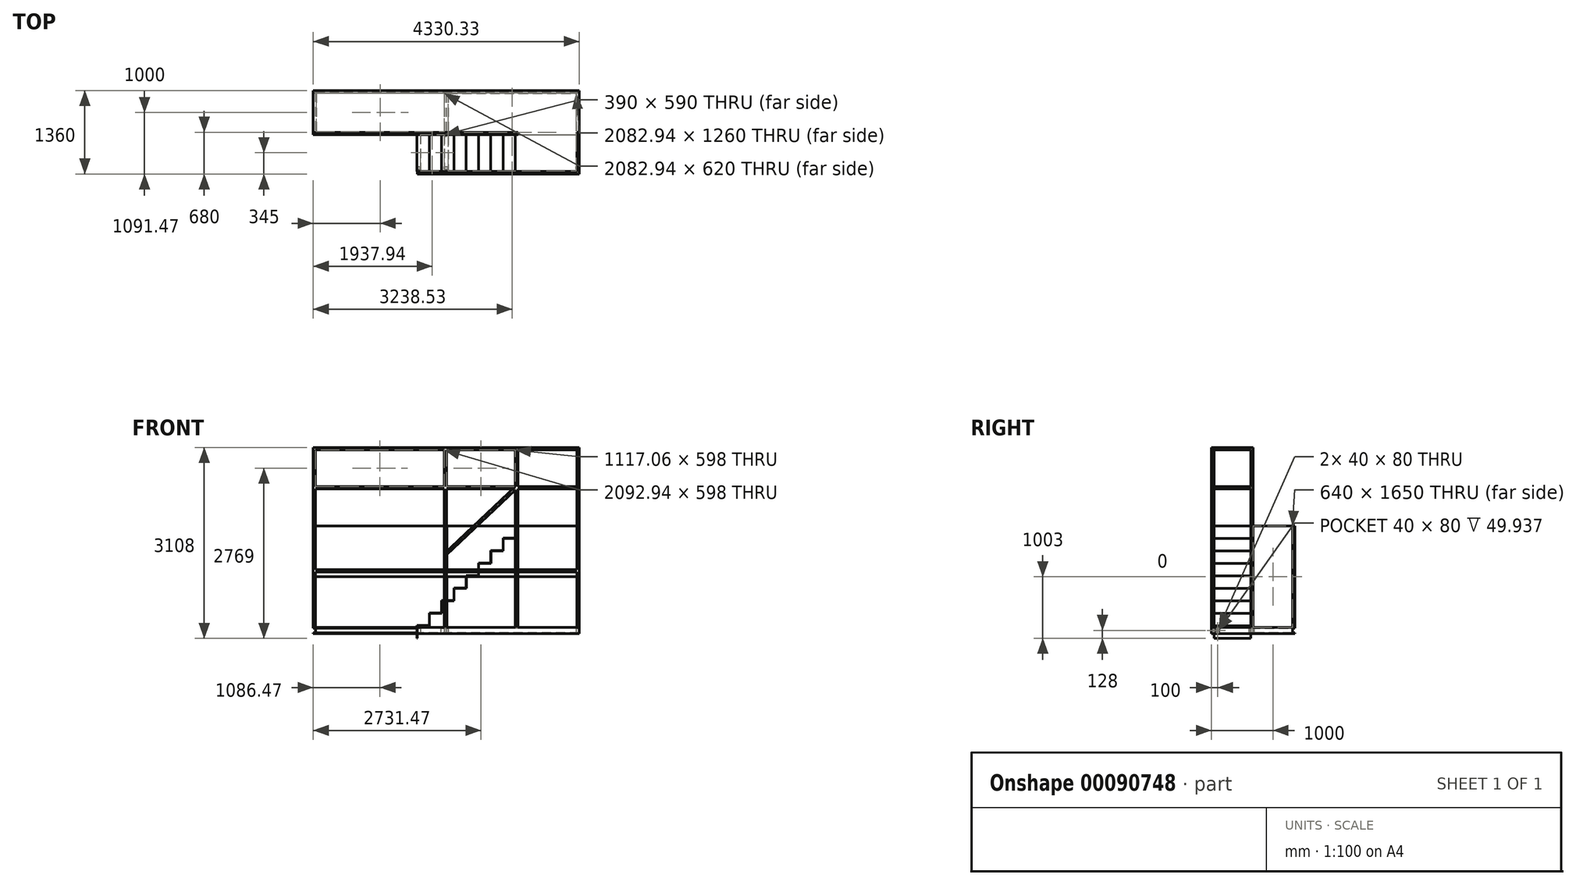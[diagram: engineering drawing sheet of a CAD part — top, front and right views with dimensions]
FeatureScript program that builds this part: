
annotation { "Feature Type Name" : "Feature", "Feature Type Description" : "" }
export const myFeature = defineFeature(function(context is Context, id is Id, definition is map)
    precondition{}
    {
        {
            var Q0;
            Q0=qCreatedBy(makeId("Top.planeOp"),FACE);
            var sketch = newSketch(context, id + "F0", { "sketchPlane" : qUnion([Q0])});
            skLineSegment(sketch, "E0.rect.bottom", {"start": v(2165, 680) * mm, "end": v(-2165, 680) * mm});
            skLineSegment(sketch, "E0.rect.top", {"start": v(2165, -680) * mm, "end": v(-32.06, -680) * mm});
            skLineSegment(sketch, "E0.rect.left", {"start": v(2165, 680) * mm, "end": v(2165, -680) * mm});
            skLineSegment(sketch, "E0.rect.right", {"start": v(-2165, 680) * mm, "end": v(-2165, -40) * mm});
            skPoint(sketch, "E0.rect.middle", {"position": v(0, 0) * mm});
            skLineSegment(sketch, "E1.rect.top", {"start": v(2115, -630) * mm, "end": v(32.06, -630) * mm});
            skLineSegment(sketch, "E1.rect.right", {"start": v(-2115, 630) * mm, "end": v(-2115, 10) * mm});
            skLineSegment(sketch, "E2.rect.left", {"start": v(32.06, -10) * mm, "end": v(32.06, -630) * mm});
            skLineSegment(sketch, "E2.rect.right", {"start": v(-32.06, 630) * mm, "end": v(-32.06, -680) * mm});
            skLineSegment(sketch, "E3.trimOffspring", {"start": v(-32.06, 630) * mm, "end": v(-2115, 630) * mm});
            skLineSegment(sketch, "E4", {"start": v(-2115, 10) * mm, "end": v(-32.06, 10) * mm});
            skLineSegment(sketch, "E5", {"start": v(-2165, -40) * mm, "end": v(-32.06, -40) * mm});
            skLineSegment(sketch, "E6", {"start": v(32.06, 630) * mm, "end": v(2115, 630) * mm});
            skLineSegment(sketch, "E7", {"start": v(2115, 630) * mm, "end": v(2115, -630) * mm});
            skLineSegment(sketch, "E8", {"start": v(32.06, 630) * mm, "end": v(32.06, -10) * mm});
            skLineSegment(sketch, "E9", {"start": v(-32.06, -680) * mm, "end": v(-472.06, -680) * mm});
            skLineSegment(sketch, "E10", {"start": v(-472.06, -680) * mm, "end": v(-472.06, -630) * mm});
            skLineSegment(sketch, "E11", {"start": v(-472.06, -630) * mm, "end": v(-32.06, -630) * mm});
            skLineSegment(sketch, "E12", {"start": v(-472.06, -630) * mm, "end": v(-472.06, -40) * mm});
            skLineSegment(sketch, "E13", {"start": v(-472.06, -40) * mm, "end": v(-422.06, -40) * mm});
            skLineSegment(sketch, "E14", {"start": v(-422.06, -40) * mm, "end": v(-422.06, -630) * mm});
            skSolve(sketch);
        }
        {
            var Q0;
            Q0=makeQuery(id+"F0.imprint","IMPRINT",FACE,{"disambiguationData":[TD([[makeQuery(id+"F0.imprint","IMPRINT",EDGE,{"derivedFrom":sQuery(id+"F0.wireOp",EDGE,"E0.rect.bottom")}),1.0]])]});
            var Q1;
            {var subQ0=sQuery(id+"F0.wireOp",EDGE,"E4");Q1=makeQuery(id+"F0.imprint","IMPRINT",FACE,{"disambiguationData":[TD([[makeQuery(id+"F0.imprint","IMPRINT",EDGE,{"derivedFrom":subQ0}),-1.0]])]});}
            var Q2;
            {var subQ0=sQuery(id+"F0.wireOp",EDGE,"E12");Q2=makeQuery(id+"F0.imprint","IMPRINT",FACE,{"disambiguationData":[TD([[makeQuery(id+"F0.imprint","IMPRINT",EDGE,{"derivedFrom":subQ0}),-1.0]])]});}
            var Q3;
            {var subQ3=sQuery(id+"F0.wireOp",EDGE,"E9");Q3=makeQuery(id+"F0.imprint","IMPRINT",FACE,{"disambiguationData":[TD([[makeQuery(id+"F0.imprint","IMPRINT",EDGE,{"derivedFrom":subQ3}),-1.0]])]});}
            extrude(context, id + "F1", {"entities" : qUnion([Q0, Q1, Q2, Q3]), "depth" : 100 * mm});
        }
        {
            var Q0;
            Q0=makeQuery(id+"F1.opExtrude","SWEPT_FACE",FACE,{"disambiguationData":[OSD([sQuery(id+"F0.wireOp",EDGE,"E0.rect.right")])]});
            var sketch = newSketch(context, id + "F2", { "sketchPlane" : qUnion([Q0])});
            skLineSegment(sketch, "E15.bottom", {"start": v(-680, 90) * mm, "end": v(-640, 90) * mm});
            skLineSegment(sketch, "E15.top", {"start": v(-680, 10) * mm, "end": v(-640, 10) * mm});
            skLineSegment(sketch, "E15.left", {"start": v(-680, 90) * mm, "end": v(-680, 10) * mm});
            skLineSegment(sketch, "E15.right", {"start": v(-640, 90) * mm, "end": v(-640, 10) * mm});
            skLineSegment(sketch, "E16.bottom", {"start": v(40, 90) * mm, "end": v(0, 90) * mm});
            skLineSegment(sketch, "E16.top", {"start": v(40, 10) * mm, "end": v(0, 10) * mm});
            skLineSegment(sketch, "E16.left", {"start": v(40, 90) * mm, "end": v(40, 10) * mm});
            skLineSegment(sketch, "E16.right", {"start": v(0, 90) * mm, "end": v(0, 10) * mm});
            skSolve(sketch);
        }
        {
            var Q0;
            Q0=makeQuery(id+"F2.imprint","IMPRINT",FACE,{"disambiguationData":[TD([[makeQuery(id+"F2.imprint","IMPRINT",EDGE,{"derivedFrom":sQuery(id+"F2.wireOp",EDGE,"E16.bottom")}),1.0]])]});
            var Q1;
            Q1=makeQuery(id+"F1.opExtrude","SWEPT_FACE",FACE,{"disambiguationData":[OSD([sQuery(id+"F0.wireOp",EDGE,"E10"),sQuery(id+"F0.wireOp",EDGE,"E12")])]});
            extrude(context, id + "F3", {"entities" : qUnion([Q0]), "operationType" : NewBodyOperationType.REMOVE, "endBound" : BoundingType.UP_TO_SURFACE, "oppositeDirection" : true, "endBoundEntityFace" : qUnion([Q1]), "depth" : 25 * mm});
        }
        {
            var Q0;
            Q0=makeQuery(id+"F2.imprint","IMPRINT",FACE,{"disambiguationData":[TD([[makeQuery(id+"F2.imprint","IMPRINT",EDGE,{"derivedFrom":sQuery(id+"F2.wireOp",EDGE,"E15.bottom")}),-1.0]])]});
            var Q1;
            {var subQ0=sQuery(id+"F0.wireOp",EDGE,"E2.rect.right");Q1=makeQuery(id+"F1.opExtrude","SWEPT_FACE",FACE,{"disambiguationData":[OSD([subQ0]),TDD([makeQuery(id+"F0.imprint","IMPRINT",EDGE,{"disambiguationData":[TD([[makeQuery(id+"F0.imprint","INTERSECT",VERTEX,{"derivedFrom":[sQuery(id+"F0.wireOp",EDGE,"E0.rect.top"),subQ0]}),1.0]])],"derivedFrom":subQ0})])]});}
            extrude(context, id + "F4", {"entities" : qUnion([Q0]), "operationType" : NewBodyOperationType.REMOVE, "endBound" : BoundingType.THROUGH_ALL, "oppositeDirection" : true, "endBoundEntityFace" : qUnion([Q1]), "depth" : 25 * mm});
        }
        {
            var Q0;
            Q0=makeQuery(id+"F3.boolean.opBoolean","COPY",FACE,{"derivedFrom":makeQuery(id+"F3.opExtrude","SWEPT_FACE",FACE,{"disambiguationData":[OSD([sQuery(id+"F2.wireOp",EDGE,"E16.right")])]})});
            var sketch = newSketch(context, id + "F5", { "sketchPlane" : qUnion([Q0])});
            skLineSegment(sketch, "E17.bottom", {"start": v(-2165, 90) * mm, "end": v(-2125, 90) * mm});
            skLineSegment(sketch, "E17.top", {"start": v(-2165, 10) * mm, "end": v(-2125, 10) * mm});
            skLineSegment(sketch, "E17.left", {"start": v(-2165, 90) * mm, "end": v(-2165, 10) * mm});
            skLineSegment(sketch, "E17.right", {"start": v(-2125, 90) * mm, "end": v(-2125, 10) * mm});
            skSolve(sketch);
        }
        {
            var Q0;
            Q0=makeQuery(id+"F5.imprint","IMPRINT",FACE,{"disambiguationData":[TD([[makeQuery(id+"F5.imprint","IMPRINT",EDGE,{"derivedFrom":sQuery(id+"F5.wireOp",EDGE,"4b8e484b-d1e7-4c6f-93f2-1164223cb3a1.bottom")}),1.0]])]});
            var Q1;
            Q1=makeQuery(id+"F5.imprint","IMPRINT",FACE,{"disambiguationData":[TD([[makeQuery(id+"F5.imprint","IMPRINT",EDGE,{"derivedFrom":sQuery(id+"F5.wireOp",EDGE,"E17.bottom")}),1.0]])]});
            var Q2;
            Q2=makeQuery(id+"F1.opExtrude","SWEPT_FACE",FACE,{"disambiguationData":[OSD([sQuery(id+"F0.wireOp",EDGE,"E3.trimOffspring")])]});
            extrude(context, id + "F6", {"entities" : qUnion([Q0, Q1]), "operationType" : NewBodyOperationType.REMOVE, "endBound" : BoundingType.THROUGH_ALL, "oppositeDirection" : true, "endBoundEntityFace" : qUnion([Q2]), "depth" : 25 * mm});
        }
        {
            var Q0;
            Q0=qCreatedBy(makeId("Top.planeOp"),FACE);
            cPlane(context, id + "F7", {"entities" : qUnion([Q0]), "cplaneType" : CPlaneType.OFFSET, "offset" : 1750 * mm, "width" : 150 * mm, "height" : 150 * mm});
        }
        {
            var Q0;
            Q0=qCreatedBy(makeId("Front.planeOp"),FACE);
            var sketch = newSketch(context, id + "F8", { "sketchPlane" : qUnion([Q0])});
            skLineSegment(sketch, "E18.bottom", {"start": v(0, 10) * mm, "end": v(-90, 10) * mm});
            skLineSegment(sketch, "E18.top", {"start": v(0, 90) * mm, "end": v(-90, 90) * mm});
            skLineSegment(sketch, "E18.left", {"start": v(0, 10) * mm, "end": v(0, 90) * mm});
            skLineSegment(sketch, "E18.right", {"start": v(-90, 10) * mm, "end": v(-90, 90) * mm});
            skSolve(sketch);
        }
        {
            var Q0;
            Q0=qSketchRegion(id+"F8",true);
            var Q1;
            Q1=makeQuery(id+"F1.opExtrude","SWEPT_FACE",FACE,{"disambiguationData":[OSD([sQuery(id+"F0.wireOp",EDGE,"E3.trimOffspring")])]});
            extrude(context, id + "F9", {"entities" : qUnion([Q0]), "operationType" : NewBodyOperationType.REMOVE, "endBound" : BoundingType.UP_TO_SURFACE, "oppositeDirection" : true, "endBoundEntityFace" : qUnion([Q1]), "depth" : 25 * mm, "hasSecondDirection" : true, "secondDirectionOppositeDirection" : false, "secondDirectionDepth" : 70 * mm});
        }
        {
            var Q0;
            Q0=makeQuery(id+"F1.opExtrude","CAP_FACE",FACE,{"disambiguationData":[OSD([sQuery(id+"F0.wireOp",EDGE,"E0.rect.bottom"),sQuery(id+"F0.wireOp",EDGE,"E0.rect.top"),sQuery(id+"F0.wireOp",EDGE,"E0.rect.left"),sQuery(id+"F0.wireOp",EDGE,"E0.rect.right"),sQuery(id+"F0.wireOp",EDGE,"E1.rect.bottom"),sQuery(id+"F0.wireOp",EDGE,"E1.rect.top"),sQuery(id+"F0.wireOp",EDGE,"E1.rect.left"),sQuery(id+"F0.wireOp",EDGE,"E1.rect.right"),sQuery(id+"F0.wireOp",EDGE,"E2.rect.left"),sQuery(id+"F0.wireOp",EDGE,"E2.rect.right"),sQuery(id+"F0.wireOp",EDGE,"E3.trimOffspring"),sQuery(id+"F0.wireOp",EDGE,"1f8814e2-eb1b-4eeb-ad56-086a4f51f8e6.trimOffspring")])],"isStart":false});
            var sketch = newSketch(context, id + "F10", { "sketchPlane" : qUnion([Q0])});
            skLineSegment(sketch, "E19.bottom", {"start": v(-2165, 680) * mm, "end": v(-2125, 680) * mm});
            skLineSegment(sketch, "E19.top", {"start": v(-2165, 640) * mm, "end": v(-2125, 640) * mm});
            skLineSegment(sketch, "E19.left", {"start": v(-2165, 680) * mm, "end": v(-2165, 640) * mm});
            skLineSegment(sketch, "E19.right", {"start": v(-2125, 680) * mm, "end": v(-2125, 640) * mm});
            skLineSegment(sketch, "E20.bottom", {"start": v(2165, 680) * mm, "end": v(2125, 680) * mm});
            skLineSegment(sketch, "E20.top", {"start": v(2165, 640) * mm, "end": v(2125, 640) * mm});
            skLineSegment(sketch, "E20.left", {"start": v(2165, 680) * mm, "end": v(2165, 640) * mm});
            skLineSegment(sketch, "E20.right", {"start": v(2125, 680) * mm, "end": v(2125, 640) * mm});
            skLineSegment(sketch, "E21.bottom", {"start": v(-27.06, 680) * mm, "end": v(12.94, 680) * mm});
            skLineSegment(sketch, "E21.top", {"start": v(-27.06, 640) * mm, "end": v(12.94, 640) * mm});
            skLineSegment(sketch, "E21.left", {"start": v(-27.06, 680) * mm, "end": v(-27.06, 640) * mm});
            skLineSegment(sketch, "E21.right", {"start": v(12.94, 680) * mm, "end": v(12.94, 640) * mm});
            skLineSegment(sketch, "E22.bottom", {"start": v(-2165, 0) * mm, "end": v(-2125, 0) * mm});
            skLineSegment(sketch, "E22.top", {"start": v(-2165, -40) * mm, "end": v(-2125, -40) * mm});
            skLineSegment(sketch, "E22.left", {"start": v(-2165, 0) * mm, "end": v(-2165, -40) * mm});
            skLineSegment(sketch, "E22.right", {"start": v(-2125, 0) * mm, "end": v(-2125, -40) * mm});
            skLineSegment(sketch, "E23.bottom", {"start": v(-32.06, 0) * mm, "end": v(7.94, 0) * mm});
            skLineSegment(sketch, "E23.top", {"start": v(-32.06, -40) * mm, "end": v(7.94, -40) * mm});
            skLineSegment(sketch, "E23.left", {"start": v(-32.06, 0) * mm, "end": v(-32.06, -40) * mm});
            skLineSegment(sketch, "E23.right", {"start": v(7.94, 0) * mm, "end": v(7.94, -40) * mm});
            skLineSegment(sketch, "E24.bottom", {"start": v(2165, 0) * mm, "end": v(2125, 0) * mm});
            skLineSegment(sketch, "E24.top", {"start": v(2165, -40) * mm, "end": v(2125, -40) * mm});
            skLineSegment(sketch, "E24.left", {"start": v(2165, 0) * mm, "end": v(2165, -40) * mm});
            skLineSegment(sketch, "E24.right", {"start": v(2125, 0) * mm, "end": v(2125, -40) * mm});
            skSolve(sketch);
        }
        {
            var Q0;
            Q0=makeQuery(id+"F10.imprint","IMPRINT",FACE,{"disambiguationData":[TD([[makeQuery(id+"F10.imprint","IMPRINT",EDGE,{"derivedFrom":sQuery(id+"F10.wireOp",EDGE,"E22.bottom")}),-1.0]])]});
            var Q1;
            Q1=makeQuery(id+"F10.imprint","IMPRINT",FACE,{"disambiguationData":[TD([[makeQuery(id+"F10.imprint","IMPRINT",EDGE,{"derivedFrom":sQuery(id+"F10.wireOp",EDGE,"E23.bottom")}),-1.0]])]});
            var Q2;
            Q2=makeQuery(id+"F10.imprint","IMPRINT",FACE,{"disambiguationData":[TD([[makeQuery(id+"F10.imprint","IMPRINT",EDGE,{"derivedFrom":sQuery(id+"F10.wireOp",EDGE,"E24.bottom")}),1.0]])]});
            extrude(context, id + "F11", {"entities" : qUnion([Q0, Q1, Q2]), "operationType" : NewBodyOperationType.ADD, "depth" : 2930 * mm});
        }
        {
            var Q0;
            Q0=qCreatedBy(id+"F7.planeOp",FACE);
            var sketch = newSketch(context, id + "F12", { "sketchPlane" : qUnion([Q0])});
            skLineSegment(sketch, "E25.bottom", {"start": v(-2165, 680) * mm, "end": v(2165, 680) * mm});
            skLineSegment(sketch, "E25.top", {"start": v(-2165, -40) * mm, "end": v(2165, -40) * mm});
            skLineSegment(sketch, "E25.left", {"start": v(-2165, 680) * mm, "end": v(-2165, -40) * mm});
            skLineSegment(sketch, "E25.right", {"start": v(2165, 680) * mm, "end": v(2165, -40) * mm});
            skSolve(sketch);
        }
        {
            var Q0;
            Q0=qSketchRegion(id+"F12",true);
            extrude(context, id + "F13", {"entities" : qUnion([Q0]), "operationType" : NewBodyOperationType.ADD, "depth" : 4 * mm});
        }
        {
            var Q0;
            Q0=qSketchRegion(id+"F10",true);
            extrude(context, id + "F14", {"entities" : qUnion([Q0]), "operationType" : NewBodyOperationType.ADD, "depth" : 1650 * mm});
        }
        {
            var Q0;
            {var subQ1=sQuery(id+"F0.wireOp",EDGE,"E0.rect.left");Q0=makeQuery(id+"F13.boolean.opBoolean","MERGE",FACE,{"derivedFrom":[makeQuery(id+"F11.boolean.opBoolean","MERGE",FACE,{"derivedFrom":[makeQuery(id+"F6.boolean.opBoolean","SPLIT",FACE,{"disambiguationData":[TD([makeQuery(id+"F3.boolean.opBoolean","COPY",FACE,{"derivedFrom":makeQuery(id+"F3.opExtrude","SWEPT_FACE",FACE,{"disambiguationData":[OSD([sQuery(id+"F2.wireOp",EDGE,"E15.bottom")])]})})])],"derivedFrom":makeQuery(id+"F1.opExtrude","SWEPT_FACE",FACE,{"disambiguationData":[OSD([subQ1])]})}),makeQuery(id+"F11.opExtrude","SWEPT_FACE",FACE,{"disambiguationData":[OSD([sQuery(id+"F10.wireOp",EDGE,"E20.left")])]}),makeQuery(id+"F11.opExtrude","SWEPT_FACE",FACE,{"disambiguationData":[OSD([sQuery(id+"F10.wireOp",EDGE,"E24.left")])]})]}),makeQuery(id+"F13.opExtrude","SWEPT_FACE",FACE,{"disambiguationData":[OSD([sQuery(id+"F12.wireOp",EDGE,"E25.right")])]})]});}
            var sketch = newSketch(context, id + "F15", { "sketchPlane" : qUnion([Q0])});
            skLineSegment(sketch, "E26.bottom", {"start": v(-40, 3030) * mm, "end": v(0, 3030) * mm});
            skLineSegment(sketch, "E26.top", {"start": v(-40, 2990) * mm, "end": v(0, 2990) * mm});
            skLineSegment(sketch, "E26.left", {"start": v(0, 3030) * mm, "end": v(0, 2990) * mm});
            skLineSegment(sketch, "E26.right", {"start": v(-40, 3030) * mm, "end": v(-40, 2990) * mm});
            skLineSegment(sketch, "E27.left", {"start": v(680, 1040) * mm, "end": v(680, 925) * mm});
            skLineSegment(sketch, "E27.right", {"start": v(0, 1040) * mm, "end": v(0, 1000) * mm});
            skLineSegment(sketch, "E28.bottom", {"start": v(-40, 1040) * mm, "end": v(0, 1040) * mm});
            skLineSegment(sketch, "E28.top", {"start": v(-40, 1000) * mm, "end": v(0, 1000) * mm});
            skLineSegment(sketch, "E28.right", {"start": v(-40, 1040) * mm, "end": v(-40, 1000) * mm});
            skLineSegment(sketch, "E29.bottom", {"start": v(-40, 2392) * mm, "end": v(0, 2392) * mm});
            skLineSegment(sketch, "E29.top", {"start": v(-40, 2352) * mm, "end": v(0, 2352) * mm});
            skLineSegment(sketch, "E29.left", {"start": v(0, 2392) * mm, "end": v(0, 2352) * mm});
            skLineSegment(sketch, "E29.right", {"start": v(-40, 2392) * mm, "end": v(-40, 2352) * mm});
            skLineSegment(sketch, "E30", {"start": v(640, 1040) * mm, "end": v(680, 1040) * mm});
            skLineSegment(sketch, "E31", {"start": v(640, 1040) * mm, "end": v(640, 925) * mm});
            skLineSegment(sketch, "E32", {"start": v(680, 925) * mm, "end": v(640, 925) * mm});
            skSolve(sketch);
        }
        {
            var Q0;
            Q0=qSketchRegion(id+"F15",true);
            extrude(context, id + "F16", {"entities" : qUnion([Q0]), "operationType" : NewBodyOperationType.ADD, "oppositeDirection" : true, "depth" : 4300 * mm});
        }
        {
            var Q0;
            Q0=makeQuery(id+"F16.boolean.opBoolean","MERGE",FACE,{"derivedFrom":[makeQuery(id+"F13.boolean.opBoolean","MERGE",FACE,{"derivedFrom":[makeQuery(id+"F11.opExtrude","SWEPT_FACE",FACE,{"disambiguationData":[OSD([sQuery(id+"F10.wireOp",EDGE,"E22.top")])]}),makeQuery(id+"F11.opExtrude","SWEPT_FACE",FACE,{"disambiguationData":[OSD([sQuery(id+"F10.wireOp",EDGE,"E23.top")])]}),makeQuery(id+"F11.opExtrude","SWEPT_FACE",FACE,{"disambiguationData":[OSD([sQuery(id+"F10.wireOp",EDGE,"E24.top")])]}),makeQuery(id+"F13.opExtrude","SWEPT_FACE",FACE,{"disambiguationData":[OSD([sQuery(id+"F12.wireOp",EDGE,"E25.top")])]})]}),makeQuery(id+"F16.opExtrude","SWEPT_FACE",FACE,{"disambiguationData":[OSD([sQuery(id+"F15.wireOp",EDGE,"E26.right")])]}),makeQuery(id+"F16.opExtrude","SWEPT_FACE",FACE,{"disambiguationData":[OSD([sQuery(id+"F15.wireOp",EDGE,"E28.right")])]}),makeQuery(id+"F16.opExtrude","SWEPT_FACE",FACE,{"disambiguationData":[OSD([sQuery(id+"F15.wireOp",EDGE,"E29.right")])]})]});
            var sketch = newSketch(context, id + "F17", { "sketchPlane" : qUnion([Q0])});
            skLineSegment(sketch, "E33.left", {"start": v(2125, 3030) * mm, "end": v(2125, 2990) * mm});
            skLineSegment(sketch, "E33.right", {"start": v(2165, 3030) * mm, "end": v(2165, 2990) * mm});
            skLineSegment(sketch, "E34", {"start": v(2125, 3030) * mm, "end": v(2165, 3030) * mm});
            skLineSegment(sketch, "E35", {"start": v(2165, 2990) * mm, "end": v(2125, 2990) * mm});
            skLineSegment(sketch, "E36", {"start": v(2125, 2392) * mm, "end": v(2165, 2392) * mm});
            skLineSegment(sketch, "E37", {"start": v(2165, 2392) * mm, "end": v(2165, 2352) * mm});
            skLineSegment(sketch, "E38", {"start": v(2165, 2352) * mm, "end": v(2125, 2352) * mm});
            skLineSegment(sketch, "E39", {"start": v(2125, 2352) * mm, "end": v(2125, 2392) * mm});
            skSolve(sketch);
        }
        {
            var Q0;
            {var subQ56=sQuery(id+"F17.wireOp",EDGE,"E33.left");Q0=makeQuery(id+"F17.imprint","IMPRINT",FACE,{"disambiguationData":[TD([[makeQuery(id+"F17.imprint","IMPRINT",EDGE,{"derivedFrom":subQ56}),-1.0]])]});}
            cPlane(context, id + "F18", {"entities" : qUnion([Q0]), "cplaneType" : CPlaneType.OFFSET, "offset" : 0 * mm, "width" : 150 * mm, "height" : 150 * mm});
        }
        {
            var Q0;
            Q0=qCreatedBy(id+"F18.planeOp",FACE);
            var sketch = newSketch(context, id + "F19", { "sketchPlane" : qUnion([Q0])});
            skLineSegment(sketch, "E40", {"start": v(2125, 1754) * mm, "end": v(1125, 1754) * mm});
            skLineSegment(sketch, "E41", {"start": v(1125, 1754) * mm, "end": v(1125, 1551) * mm});
            skLineSegment(sketch, "E42", {"start": v(1125, 1551) * mm, "end": v(925, 1551) * mm});
            skLineSegment(sketch, "E43", {"start": v(925, 1551) * mm, "end": v(925, 1348) * mm});
            skLineSegment(sketch, "E44", {"start": v(925, 1348) * mm, "end": v(725, 1348) * mm});
            skLineSegment(sketch, "E45", {"start": v(725, 1348) * mm, "end": v(725, 1145) * mm});
            skLineSegment(sketch, "E46", {"start": v(725, 1145) * mm, "end": v(525, 1145) * mm});
            skLineSegment(sketch, "E47", {"start": v(525, 1145) * mm, "end": v(525, 942) * mm});
            skLineSegment(sketch, "E48", {"start": v(525, 942) * mm, "end": v(325, 942) * mm});
            skLineSegment(sketch, "E49", {"start": v(325, 942) * mm, "end": v(325, 739) * mm});
            skLineSegment(sketch, "E50", {"start": v(325, 739) * mm, "end": v(125, 739) * mm});
            skLineSegment(sketch, "E51", {"start": v(125, 739) * mm, "end": v(125, 536) * mm});
            skLineSegment(sketch, "E52", {"start": v(125, 536) * mm, "end": v(-75, 536) * mm});
            skLineSegment(sketch, "E53", {"start": v(-75, 536) * mm, "end": v(-75, 333) * mm});
            skLineSegment(sketch, "E54", {"start": v(-75, 333) * mm, "end": v(-275, 333) * mm});
            skLineSegment(sketch, "E55", {"start": v(-275, 333) * mm, "end": v(-275, 130) * mm});
            skLineSegment(sketch, "E56", {"start": v(-275, 130) * mm, "end": v(-475, 130) * mm});
            skLineSegment(sketch, "E57", {"start": v(-475, 130) * mm, "end": v(-475, -75) * mm});
            skLineSegment(sketch, "E58", {"start": v(-472, -78) * mm, "end": v(-472, 127) * mm});
            skLineSegment(sketch, "E59", {"start": v(-472, 127) * mm, "end": v(-272, 127) * mm});
            skLineSegment(sketch, "E60", {"start": v(-272, 127) * mm, "end": v(-272, 330) * mm});
            skLineSegment(sketch, "E61", {"start": v(-272, 330) * mm, "end": v(-72, 330) * mm});
            skLineSegment(sketch, "E62", {"start": v(-72, 330) * mm, "end": v(-72, 533) * mm});
            skLineSegment(sketch, "E63", {"start": v(-72, 533) * mm, "end": v(128, 533) * mm});
            skLineSegment(sketch, "E64", {"start": v(128, 533) * mm, "end": v(128, 736) * mm});
            skLineSegment(sketch, "E65", {"start": v(128, 736) * mm, "end": v(328, 736) * mm});
            skLineSegment(sketch, "E66", {"start": v(328, 736) * mm, "end": v(328, 939) * mm});
            skLineSegment(sketch, "E67", {"start": v(328, 939) * mm, "end": v(528, 939) * mm});
            skLineSegment(sketch, "E68", {"start": v(528, 939) * mm, "end": v(528, 1142) * mm});
            skLineSegment(sketch, "E69", {"start": v(528, 1142) * mm, "end": v(728, 1142) * mm});
            skLineSegment(sketch, "E70", {"start": v(728, 1142) * mm, "end": v(728, 1345) * mm});
            skLineSegment(sketch, "E71", {"start": v(728, 1345) * mm, "end": v(928, 1345) * mm});
            skLineSegment(sketch, "E72", {"start": v(928, 1345) * mm, "end": v(928, 1548) * mm});
            skLineSegment(sketch, "E73", {"start": v(928, 1548) * mm, "end": v(1128, 1548) * mm});
            skLineSegment(sketch, "E74", {"start": v(1128, 1548) * mm, "end": v(1128, 1751) * mm});
            skLineSegment(sketch, "E75", {"start": v(1128, 1751) * mm, "end": v(2125, 1751) * mm});
            skLineSegment(sketch, "E76", {"start": v(2125, 1751) * mm, "end": v(2125, 1754) * mm});
            skLineSegment(sketch, "E77", {"start": v(-475, -75) * mm, "end": v(-472, -78) * mm});
            skSolve(sketch);
        }
        {
            var Q0;
            Q0=makeQuery(id+"F19.imprint","IMPRINT",FACE,{"disambiguationData":[TD([[makeQuery(id+"F19.imprint","IMPRINT",EDGE,{"derivedFrom":sQuery(id+"F19.wireOp",EDGE,"E40")}),1.0]])]});
            extrude(context, id + "F20", {"entities" : qUnion([Q0]), "operationType" : NewBodyOperationType.ADD, "depth" : 600 * mm});
        }
        {
            var Q0;
            Q0=makeQuery(id+"F1.opExtrude","CAP_FACE",FACE,{"disambiguationData":[OSD([sQuery(id+"F0.wireOp",EDGE,"E0.rect.bottom"),sQuery(id+"F0.wireOp",EDGE,"E0.rect.top"),sQuery(id+"F0.wireOp",EDGE,"E0.rect.left"),sQuery(id+"F0.wireOp",EDGE,"E0.rect.right"),sQuery(id+"F0.wireOp",EDGE,"E1.rect.top"),sQuery(id+"F0.wireOp",EDGE,"E1.rect.right"),sQuery(id+"F0.wireOp",EDGE,"E2.rect.left"),sQuery(id+"F0.wireOp",EDGE,"E2.rect.right"),sQuery(id+"F0.wireOp",EDGE,"E3.trimOffspring"),sQuery(id+"F0.wireOp",EDGE,"E4"),sQuery(id+"F0.wireOp",EDGE,"E5"),sQuery(id+"F0.wireOp",EDGE,"E6"),sQuery(id+"F0.wireOp",EDGE,"E7"),sQuery(id+"F0.wireOp",EDGE,"E8"),sQuery(id+"F0.wireOp",EDGE,"E9"),sQuery(id+"F0.wireOp",EDGE,"E10"),sQuery(id+"F0.wireOp",EDGE,"E11"),sQuery(id+"F0.wireOp",EDGE,"E12"),sQuery(id+"F0.wireOp",EDGE,"E14")])],"isStart":false});
            var sketch = newSketch(context, id + "F21", { "sketchPlane" : qUnion([Q0])});
            skLineSegment(sketch, "E78.bottom", {"start": v(7.94, -680) * mm, "end": v(-32.06, -680) * mm});
            skLineSegment(sketch, "E78.top", {"start": v(7.94, -640) * mm, "end": v(-32.06, -640) * mm});
            skLineSegment(sketch, "E78.left", {"start": v(7.94, -680) * mm, "end": v(7.94, -640) * mm});
            skLineSegment(sketch, "E78.right", {"start": v(-32.06, -680) * mm, "end": v(-32.06, -640) * mm});
            skLineSegment(sketch, "E79.bottom", {"start": v(1125, -680) * mm, "end": v(1165, -680) * mm});
            skLineSegment(sketch, "E79.top", {"start": v(1125, -640) * mm, "end": v(1165, -640) * mm});
            skLineSegment(sketch, "E79.left", {"start": v(1125, -680) * mm, "end": v(1125, -640) * mm});
            skLineSegment(sketch, "E79.right", {"start": v(1165, -680) * mm, "end": v(1165, -640) * mm});
            skLineSegment(sketch, "E80.bottom", {"start": v(2165, -680) * mm, "end": v(2125, -680) * mm});
            skLineSegment(sketch, "E80.top", {"start": v(2165, -640) * mm, "end": v(2125, -640) * mm});
            skLineSegment(sketch, "E80.left", {"start": v(2165, -680) * mm, "end": v(2165, -640) * mm});
            skLineSegment(sketch, "E80.right", {"start": v(2125, -680) * mm, "end": v(2125, -640) * mm});
            skSolve(sketch);
        }
        {
            var Q0;
            Q0=makeQuery(id+"F21.imprint","IMPRINT",FACE,{"disambiguationData":[TD([[makeQuery(id+"F21.imprint","IMPRINT",EDGE,{"derivedFrom":sQuery(id+"F21.wireOp",EDGE,"E79.bottom")}),-1.0]])]});
            extrude(context, id + "F22", {"entities" : qUnion([Q0]), "operationType" : NewBodyOperationType.ADD, "depth" : 2930 * mm});
        }
        {
            var Q0;
            Q0=makeQuery(id+"F21.imprint","IMPRINT",FACE,{"disambiguationData":[TD([[makeQuery(id+"F21.imprint","IMPRINT",EDGE,{"derivedFrom":sQuery(id+"F21.wireOp",EDGE,"E78.bottom")}),-1.0]])]});
            extrude(context, id + "F23", {"entities" : qUnion([Q0]), "operationType" : NewBodyOperationType.ADD, "depth" : 1200 * mm});
        }
        {
            var Q0;
            Q0=makeQuery(id+"F23.boolean.opBoolean","MERGE",FACE,{"derivedFrom":[makeQuery(id+"F1.opExtrude","SWEPT_FACE",FACE,{"disambiguationData":[OSD([sQuery(id+"F0.wireOp",EDGE,"E0.rect.top"),sQuery(id+"F0.wireOp",EDGE,"E9")])]}),makeQuery(id+"F23.opExtrude","SWEPT_FACE",FACE,{"disambiguationData":[OSD([sQuery(id+"F21.wireOp",EDGE,"E78.bottom")])]})]});
            var sketch = newSketch(context, id + "F24", { "sketchPlane" : qUnion([Q0])});
            skLineSegment(sketch, "E81", {"start": v(-32.06, 1300) * mm, "end": v(1125, 2392.7) * mm});
            skLineSegment(sketch, "E82", {"start": v(1125, 2337.69) * mm, "end": v(7.94, 1282.76) * mm});
            skLineSegment(sketch, "E83", {"start": v(-32.06, 1300) * mm, "end": v(7.94, 1282.76) * mm});
            skLineSegment(sketch, "E84", {"start": v(1125, 2392.7) * mm, "end": v(1125, 2337.69) * mm});
            skLineSegment(sketch, "E85", {"start": v(1125, 2392.7) * mm, "end": v(2165.33, 2392.7) * mm});
            skLineSegment(sketch, "E86", {"start": v(2165.33, 2392.7) * mm, "end": v(2165.33, 2352.7) * mm});
            skLineSegment(sketch, "E87", {"start": v(2165.33, 2352.7) * mm, "end": v(1125, 2352.7) * mm});
            skLineSegment(sketch, "E88", {"start": v(1125, 2352.7) * mm, "end": v(1125, 2392.7) * mm});
            skLineSegment(sketch, "E89", {"start": v(1125, 3030) * mm, "end": v(2165, 3030) * mm});
            skLineSegment(sketch, "E90", {"start": v(2165, 3030) * mm, "end": v(2165, 2990) * mm});
            skLineSegment(sketch, "E91", {"start": v(2165, 2990) * mm, "end": v(1125, 2990) * mm});
            skLineSegment(sketch, "E92", {"start": v(1125, 3030) * mm, "end": v(1125, 2990) * mm});
            skSolve(sketch);
        }
        {
            var Q0;
            {var subQ2=sQuery(id+"F21.wireOp",EDGE,"E78.bottom");var subQ8=makeQuery(id+"F23.opExtrude","CAP_EDGE",EDGE,{"disambiguationData":[OSD([subQ2])],"isStart":false});Q0=makeQuery(id+"F24.imprint","IMPRINT",FACE,{"disambiguationData":[TD([[makeQuery(id+"F24.imprint","IMPRINT",EDGE,{"derivedFrom":subQ8}),-1.0]])]});}
            var Q1;
            {var subQ0=sQuery(id+"F24.wireOp",EDGE,"E85");var subQ1=sQuery(id+"F0.wireOp",EDGE,"E0.rect.top");var subQ2=makeQuery(id+"F22.opExtrude","SWEPT_EDGE",EDGE,{"disambiguationData":[OSD([subQ1,sQuery(id+"F21.wireOp",EDGE,"E79.bottom"),sQuery(id+"F21.wireOp",EDGE,"E79.right")])]});var subQ3=makeQuery(id+"F24.imprint","INTERSECT",VERTEX,{"derivedFrom":[subQ2,subQ0]});Q1=makeQuery(id+"F24.imprint","IMPRINT",FACE,{"disambiguationData":[TD([[makeQuery(id+"F24.imprint","IMPRINT",EDGE,{"disambiguationData":[TD([[subQ3,-1.0]])],"derivedFrom":subQ0}),-1.0]])]});}
            var Q2;
            {var subQ0=sQuery(id+"F24.wireOp",EDGE,"E89");var subQ1=sQuery(id+"F0.wireOp",EDGE,"E0.rect.top");var subQ2=makeQuery(id+"F22.opExtrude","SWEPT_EDGE",EDGE,{"disambiguationData":[OSD([subQ1,sQuery(id+"F21.wireOp",EDGE,"E79.bottom"),sQuery(id+"F21.wireOp",EDGE,"E79.right")])]});var subQ3=makeQuery(id+"F24.imprint","INTERSECT",VERTEX,{"derivedFrom":[subQ2,subQ0]});var subQ4=makeQuery(id+"F22.opExtrude","SWEPT_EDGE",EDGE,{"disambiguationData":[OSD([subQ1,sQuery(id+"F21.wireOp",EDGE,"E80.bottom"),sQuery(id+"F21.wireOp",EDGE,"E80.right")])]});var subQ5=makeQuery(id+"F24.imprint","INTERSECT",VERTEX,{"derivedFrom":[subQ4,subQ0]});Q2=makeQuery(id+"F24.imprint","IMPRINT",FACE,{"disambiguationData":[TD([[makeQuery(id+"F24.imprint","IMPRINT",EDGE,{"disambiguationData":[TD([[subQ3,-1.0],[subQ5,1.0]])],"derivedFrom":subQ0}),-1.0]])]});}
            extrude(context, id + "F25", {"entities" : qUnion([Q0, Q1, Q2]), "operationType" : NewBodyOperationType.ADD, "oppositeDirection" : true, "depth" : 40 * mm});
        }
        {
            var Q0;
            Q0=makeQuery(id+"F17.imprint","IMPRINT",FACE,{"disambiguationData":[TD([[makeQuery(id+"F17.imprint","IMPRINT",EDGE,{"derivedFrom":sQuery(id+"F17.wireOp",EDGE,"E36")}),-1.0]])]});
            var Q1;
            Q1=makeQuery(id+"F17.imprint","IMPRINT",FACE,{"disambiguationData":[TD([[makeQuery(id+"F17.imprint","IMPRINT",EDGE,{"derivedFrom":sQuery(id+"F17.wireOp",EDGE,"E33.left")}),1.0]])]});
            extrude(context, id + "F26", {"entities" : qUnion([Q0, Q1]), "operationType" : NewBodyOperationType.ADD, "depth" : 610 * mm});
        }
        {
            var Q0;
            Q0=makeQuery(id+"F20.boolean.opBoolean","MERGE",FACE,{"derivedFrom":[makeQuery(id+"F13.opExtrude","CAP_FACE",FACE,{"disambiguationData":[OSD([sQuery(id+"F12.wireOp",EDGE,"E25.bottom"),sQuery(id+"F12.wireOp",EDGE,"E25.top"),sQuery(id+"F12.wireOp",EDGE,"E25.left"),sQuery(id+"F12.wireOp",EDGE,"E25.right")])],"isStart":false}),makeQuery(id+"F20.opExtrude","SWEPT_FACE",FACE,{"disambiguationData":[OSD([sQuery(id+"F19.wireOp",EDGE,"E40")])]})]});
            var sketch = newSketch(context, id + "F27", { "sketchPlane" : qUnion([Q0])});
            skLineSegment(sketch, "E93.bottom", {"start": v(1125, -40) * mm, "end": v(1165, -40) * mm});
            skLineSegment(sketch, "E93.top", {"start": v(1125, 0) * mm, "end": v(1165, 0) * mm});
            skLineSegment(sketch, "E93.left", {"start": v(1125, -40) * mm, "end": v(1125, 0) * mm});
            skLineSegment(sketch, "E93.right", {"start": v(1165, -40) * mm, "end": v(1165, 0) * mm});
            skSolve(sketch);
        }
        {
            var Q0;
            Q0 = qSketchRegion(id + "F27", true);
            var Q1;
            Q1=makeQuery(id+"F27.imprint","IMPRINT",FACE,{"disambiguationData":[TD([[makeQuery(id+"F27.imprint","IMPRINT",EDGE,{"derivedFrom":sQuery(id+"F27.wireOp",EDGE,"E93.bottom")}),1.0]])]});
            extrude(context, id + "F28", {"entities" : qUnion([Q0, Q1]), "operationType" : NewBodyOperationType.ADD, "depth" : 1275 * mm});
        }
        {
            var Q0;
            {var subQ0=sQuery(id+"F10.wireOp",EDGE,"E24.right");var subQ1=sQuery(id+"F10.wireOp",EDGE,"E24.left");var subQ2=sQuery(id+"F10.wireOp",EDGE,"E24.bottom");var subQ6=sQuery(id+"F10.wireOp",EDGE,"E23.right");var subQ7=sQuery(id+"F10.wireOp",EDGE,"E23.left");var subQ8=sQuery(id+"F10.wireOp",EDGE,"E23.bottom");var subQ9=sQuery(id+"F10.wireOp",EDGE,"E22.right");var subQ10=sQuery(id+"F10.wireOp",EDGE,"E22.left");var subQ11=sQuery(id+"F10.wireOp",EDGE,"E22.bottom");Q0=makeQuery(id+"F28.boolean.opBoolean","MERGE",FACE,{"derivedFrom":[makeQuery(id+"F16.boolean.opBoolean","MERGE",FACE,{"derivedFrom":[makeQuery(id+"F13.boolean.opBoolean","SPLIT",FACE,{"disambiguationData":[TD([makeQuery(id+"F11.opExtrude","CAP_FACE",FACE,{"disambiguationData":[OSD([subQ11,sQuery(id+"F10.wireOp",EDGE,"E22.top"),subQ10,subQ9])],"isStart":false})])],"derivedFrom":makeQuery(id+"F11.opExtrude","SWEPT_FACE",FACE,{"disambiguationData":[OSD([subQ11])]})}),makeQuery(id+"F13.boolean.opBoolean","SPLIT",FACE,{"disambiguationData":[TD([makeQuery(id+"F11.opExtrude","CAP_FACE",FACE,{"disambiguationData":[OSD([subQ8,sQuery(id+"F10.wireOp",EDGE,"E23.top"),subQ7,subQ6])],"isStart":false})])],"derivedFrom":makeQuery(id+"F11.opExtrude","SWEPT_FACE",FACE,{"disambiguationData":[OSD([subQ8])]})}),makeQuery(id+"F13.boolean.opBoolean","SPLIT",FACE,{"disambiguationData":[TD([makeQuery(id+"F11.opExtrude","CAP_FACE",FACE,{"disambiguationData":[OSD([subQ2,sQuery(id+"F10.wireOp",EDGE,"E24.top"),subQ1,subQ0])],"isStart":false})])],"derivedFrom":makeQuery(id+"F11.opExtrude","SWEPT_FACE",FACE,{"disambiguationData":[OSD([subQ2])]})}),makeQuery(id+"F16.opExtrude","SWEPT_FACE",FACE,{"disambiguationData":[OSD([sQuery(id+"F15.wireOp",EDGE,"E26.left")])]}),makeQuery(id+"F16.opExtrude","SWEPT_FACE",FACE,{"disambiguationData":[OSD([sQuery(id+"F15.wireOp",EDGE,"E29.left")])]})]}),makeQuery(id+"F28.opExtrude","SWEPT_FACE",FACE,{"disambiguationData":[OSD([sQuery(id+"F27.wireOp",EDGE,"E93.top")])]})]});}
            var sketch = newSketch(context, id + "F29", { "sketchPlane" : qUnion([Q0])});
            skLineSegment(sketch, "E94.bottom", {"start": v(-1165, 3030) * mm, "end": v(-2125, 3030) * mm});
            skLineSegment(sketch, "E94.top", {"start": v(-1165, 1946.3) * mm, "end": v(-2125, 1946.3) * mm});
            skLineSegment(sketch, "E94.left", {"start": v(-1165, 3030) * mm, "end": v(-1165, 1946.3) * mm});
            skLineSegment(sketch, "E94.right", {"start": v(-2125, 3030) * mm, "end": v(-2125, 1946.3) * mm});
            skSolve(sketch);
        }
        {
            var Q0;
            Q0 = qSketchRegion(id + "F29", true);
            extrude(context, id + "F30", {"entities" : qUnion([Q0]), "operationType" : NewBodyOperationType.REMOVE, "oppositeDirection" : true, "depth" : 50 * mm});
        }
        {
            var Q0;
            Q0=makeQuery(id+"F26.boolean.opBoolean","MERGE",FACE,{"derivedFrom":[makeQuery(id+"F22.boolean.opBoolean","MERGE",FACE,{"derivedFrom":[makeQuery(id+"F14.boolean.opBoolean","MERGE",FACE,{"derivedFrom":[makeQuery(id+"F13.boolean.opBoolean","MERGE",FACE,{"derivedFrom":[makeQuery(id+"F11.boolean.opBoolean","MERGE",FACE,{"derivedFrom":[makeQuery(id+"F1.opExtrude","SWEPT_FACE",FACE,{"disambiguationData":[OSD([sQuery(id+"F0.wireOp",EDGE,"E0.rect.left")])]}),makeQuery(id+"F11.opExtrude","SWEPT_FACE",FACE,{"disambiguationData":[OSD([sQuery(id+"F10.wireOp",EDGE,"E24.left")])]})]}),makeQuery(id+"F13.opExtrude","SWEPT_FACE",FACE,{"disambiguationData":[OSD([sQuery(id+"F12.wireOp",EDGE,"E25.right")])]})]}),makeQuery(id+"F14.opExtrude","SWEPT_FACE",FACE,{"disambiguationData":[OSD([sQuery(id+"F10.wireOp",EDGE,"E20.left")])]})]}),makeQuery(id+"F22.opExtrude","SWEPT_FACE",FACE,{"disambiguationData":[OSD([sQuery(id+"F21.wireOp",EDGE,"E80.left")])]})]}),makeQuery(id+"F26.opExtrude","SWEPT_FACE",FACE,{"disambiguationData":[OSD([sQuery(id+"F17.wireOp",EDGE,"E33.right")])]}),makeQuery(id+"F26.opExtrude","SWEPT_FACE",FACE,{"disambiguationData":[OSD([sQuery(id+"F17.wireOp",EDGE,"E37")])]})]});
            var sketch = newSketch(context, id + "F31", { "sketchPlane" : qUnion([Q0])});
            skLineSegment(sketch, "E95", {"start": v(-600, 10) * mm, "end": v(-560, 10) * mm});
            skLineSegment(sketch, "E96", {"start": v(-560, 10) * mm, "end": v(-560, 90) * mm});
            skLineSegment(sketch, "E97", {"start": v(-560, 90) * mm, "end": v(-600, 90) * mm});
            skLineSegment(sketch, "E98", {"start": v(-600, 90) * mm, "end": v(-600, 10) * mm});
            skSolve(sketch);
        }
        {
            var Q0;
            Q0=makeQuery(id+"F31.imprint","IMPRINT",FACE,{"disambiguationData":[TD([[makeQuery(id+"F31.imprint","IMPRINT",EDGE,{"derivedFrom":sQuery(id+"F31.wireOp",EDGE,"E95")}),1.0]])]});
            var Q1;
            Q1=makeQuery(id+"F20.opExtrude","SWEPT_FACE",FACE,{"disambiguationData":[OSD([sQuery(id+"F19.wireOp",EDGE,"E58")])]});
            extrude(context, id + "F32", {"entities" : qUnion([Q0]), "operationType" : NewBodyOperationType.REMOVE, "endBound" : BoundingType.UP_TO_SURFACE, "oppositeDirection" : true, "endBoundEntityFace" : qUnion([Q1]), "depth" : 25 * mm});
        }
    });
